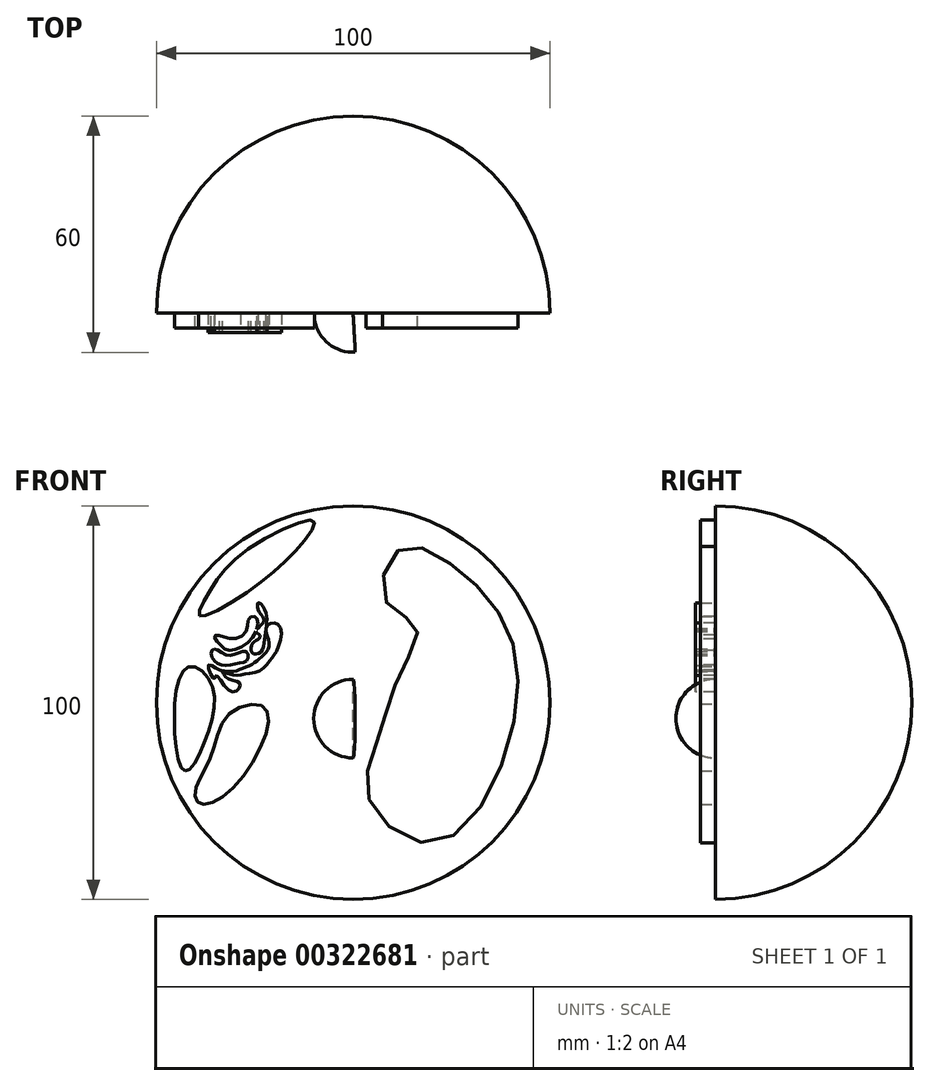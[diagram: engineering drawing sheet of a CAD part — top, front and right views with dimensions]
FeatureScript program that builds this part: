
annotation { "Feature Type Name" : "Feature", "Feature Type Description" : "" }
export const myFeature = defineFeature(function(context is Context, id is Id, definition is map)
    precondition{}
    {
        {
            var Q0;
            Q0=qCreatedBy(makeId("Front.planeOp"),FACE);
            var sketch = newSketch(context, id + "F0", { "sketchPlane" : qUnion([Q0])});
            skLineSegment(sketch, "E0", {"start": v(0, 0) * mm, "end": v(0, 100) * mm});
            skArc(sketch, "E1", {"start": v(0, 0) * mm, "mid": v(50, 50) * mm, "end": v(0, 100) * mm});
            skSolve(sketch);
        }
        {
            var Q0;
            Q0 = qSketchRegion(id + "F0", true);
            var Q1;
            Q1=makeQuery(id+"F0.imprint","IMPRINT",FACE,{"disambiguationData":[TD([[makeQuery(id+"F0.imprint","IMPRINT",EDGE,{"derivedFrom":sQuery(id+"F0.wireOp",EDGE,"E0")}),-1.0]])]});
            var Q2;
            Q2=sQuery(id+"F0.wireOp",EDGE,"E0");
            revolve(context, id + "F1", {"entities" : qUnion([Q0, Q1]), "axis" : qUnion([Q2]), "revolveType" : RevolveType.ONE_DIRECTION, "angle" : 180 * degree});
        }
        {
            var Q0;
            Q0=makeQuery(id+"F1.opRevolve","CAP_FACE",FACE,{"disambiguationData":[OSD([sQuery(id+"F0.wireOp",EDGE,"E0"),sQuery(id+"F0.wireOp",EDGE,"E1")])],"isStart":true});
            var sketch = newSketch(context, id + "F2", { "sketchPlane" : qUnion([Q0])});
            skLineSegment(sketch, "E2", {"start": v(0, 35.93) * mm, "end": v(0, 55.93) * mm});
            skArc(sketch, "E3", {"start": v(0, 55.93) * mm, "mid": v(-10, 45.93) * mm, "end": v(0, 35.93) * mm});
            skSolve(sketch);
        }
        {
            var Q0;
            Q0 = qSketchRegion(id + "F2", true);
            var Q1;
            Q1=sQuery(id+"F2.wireOp",EDGE,"E2");
            revolve(context, id + "F3", {"entities" : qUnion([Q0]), "axis" : qUnion([Q1]), "revolveType" : RevolveType.ONE_DIRECTION, "angle" : 93.1 * degree});
        }
        {
            var Q0;
            Q0=makeQuery(id+"F3.opRevolve","CAP_FACE",FACE,{"disambiguationData":[OSD([sQuery(id+"F2.wireOp",EDGE,"E2"),sQuery(id+"F2.wireOp",EDGE,"E3")])],"isStart":false});
            var sketch = newSketch(context, id + "F4", { "sketchPlane" : qUnion([Q0])});
            skLineSegment(sketch, "E4", {"start": v(0, 43.18) * mm, "end": v(0, 48.18) * mm});
            skArc(sketch, "E5", {"start": v(0, 48.18) * mm, "mid": v(-2.5, 45.68) * mm, "end": v(0, 43.18) * mm});
            skSolve(sketch);
        }
        {
            var Q0;
            Q0=sQuery(id+"F4.wireOp",EDGE,"E5");
            var Q1;
            Q1=sQuery(id+"F4.wireOp",EDGE,"E4");
            revolve(context, id + "F5", {"bodyType" : ToolBodyType.SURFACE, "surfaceEntities" : qUnion([Q0]), "axis" : qUnion([Q1]), "revolveType" : RevolveType.ONE_DIRECTION, "angle" : 86.48 * degree});
        }
        {
            var Q0;
            Q0=makeQuery(id+"F1.opRevolve","CAP_FACE",FACE,{"disambiguationData":[OSD([sQuery(id+"F0.wireOp",EDGE,"E0"),sQuery(id+"F0.wireOp",EDGE,"E1")])],"isStart":true});
            var sketch = newSketch(context, id + "F6", { "sketchPlane" : qUnion([Q0])});
            skLineSegment(sketch, "E6", {"start": v(-9.98, 15.87) * mm, "end": v(-9.98, 23.01) * mm});
            skArc(sketch, "E7", {"start": v(-9.98, 15.87) * mm, "mid": v(-6.4, 19.44) * mm, "end": v(-9.98, 23.01) * mm});
            skSolve(sketch);
        }
        {
            var Q0;
            Q0=sQuery(id+"F6.wireOp",EDGE,"E7");
            var Q1;
            Q1=sQuery(id+"F6.wireOp",EDGE,"E6");
            revolve(context, id + "F7", {"bodyType" : ToolBodyType.SURFACE, "surfaceEntities" : qUnion([Q0]), "axis" : qUnion([Q1]), "revolveType" : RevolveType.FULL});
        }
        {
            var Q0;
            Q0=makeQuery(id+"F1.opRevolve","CAP_FACE",FACE,{"disambiguationData":[OSD([sQuery(id+"F0.wireOp",EDGE,"E0"),sQuery(id+"F0.wireOp",EDGE,"E1")])],"isStart":true});
            var sketch = newSketch(context, id + "F8", { "sketchPlane" : qUnion([Q0])});
            skLineSegment(sketch, "E8", {"start": v(-1.05, 9.65) * mm, "end": v(-1.05, 18.62) * mm});
            skSolve(sketch);
        }
        {
            var Q0;
            Q0=makeQuery(id+"F8.imprint","IMPRINT",FACE,{"disambiguationData":[TD([[makeQuery(id+"F8.imprint","IMPRINT",EDGE,{"derivedFrom":makeQuery(id+"F1.opRevolve","CAP_EDGE",EDGE,{"disambiguationData":[OSD([sQuery(id+"F0.wireOp",EDGE,"E1")])],"isStart":true})}),-1.0]])]});
            var sketch = newSketch(context, id + "F9", { "sketchPlane" : qUnion([Q0])});
            skArc(sketch, "E9", {"start": v(-0.92, 9.35) * mm, "mid": v(3.57, 13.83) * mm, "end": v(-0.68, 18.54) * mm});
            skSolve(sketch);
        }
        {
            var Q0;
            Q0=sQuery(id+"F9.wireOp",EDGE,"E9");
            var Q1;
            Q1=sQuery(id+"F8.wireOp",EDGE,"E8");
            revolve(context, id + "F10", {"bodyType" : ToolBodyType.SURFACE, "surfaceEntities" : qUnion([Q0]), "axis" : qUnion([Q1]), "revolveType" : RevolveType.FULL});
        }
        {
            var Q0;
            Q0=makeQuery(id+"F1.opRevolve","CAP_FACE",FACE,{"disambiguationData":[OSD([sQuery(id+"F0.wireOp",EDGE,"E0"),sQuery(id+"F0.wireOp",EDGE,"E1")])],"isStart":true});
            var sketch = newSketch(context, id + "F11", { "sketchPlane" : qUnion([Q0])});
            skLineSegment(sketch, "E10", {"start": v(-5.22, 25.46) * mm, "end": v(-0.61, 21.85) * mm});
            skSolve(sketch);
        }
        {
            var Q0;
            Q0=makeQuery(id+"F11.imprint","IMPRINT",FACE,{"disambiguationData":[TD([[makeQuery(id+"F11.imprint","IMPRINT",EDGE,{"derivedFrom":makeQuery(id+"F1.opRevolve","CAP_EDGE",EDGE,{"disambiguationData":[OSD([sQuery(id+"F0.wireOp",EDGE,"E1")])],"isStart":true})}),-1.0]])]});
            var sketch = newSketch(context, id + "F12", { "sketchPlane" : qUnion([Q0])});
            skArc(sketch, "E11", {"start": v(-0.54, 22.14) * mm, "mid": v(-1.04, 25.86) * mm, "end": v(-4.8, 25.84) * mm});
            skSolve(sketch);
        }
        {
            var Q0;
            Q0=sQuery(id+"F12.wireOp",EDGE,"E11");
            var Q1;
            Q1=sQuery(id+"F11.wireOp",EDGE,"E10");
            revolve(context, id + "F13", {"bodyType" : ToolBodyType.SURFACE, "surfaceEntities" : qUnion([Q0]), "axis" : qUnion([Q1]), "revolveType" : RevolveType.FULL});
        }
        {
            var Q0;
            Q0=makeQuery(id+"F1.opRevolve","CAP_FACE",FACE,{"disambiguationData":[OSD([sQuery(id+"F0.wireOp",EDGE,"E0"),sQuery(id+"F0.wireOp",EDGE,"E1")])],"isStart":true});
            var sketch = newSketch(context, id + "F14", { "sketchPlane" : qUnion([Q0])});
            skLineSegment(sketch, "E12", {"start": v(-25.5, 15.6) * mm, "end": v(-20.36, 10.58) * mm});
            skSolve(sketch);
        }
        {
            var Q0;
            Q0=makeQuery(id+"F14.imprint","IMPRINT",FACE,{"disambiguationData":[TD([[makeQuery(id+"F14.imprint","IMPRINT",EDGE,{"derivedFrom":makeQuery(id+"F1.opRevolve","CAP_EDGE",EDGE,{"disambiguationData":[OSD([sQuery(id+"F0.wireOp",EDGE,"E1")])],"isStart":true})}),-1.0]])]});
            var sketch = newSketch(context, id + "F15", { "sketchPlane" : qUnion([Q0])});
            skArc(sketch, "E13", {"start": v(-20.16, 10.62) * mm, "mid": v(-20.3, 15.55) * mm, "end": v(-25.24, 15.58) * mm});
            skSolve(sketch);
        }
        {
            var Q0;
            Q0=sQuery(id+"F15.wireOp",EDGE,"E13");
            var Q1;
            Q1=sQuery(id+"F14.wireOp",EDGE,"E12");
            revolve(context, id + "F16", {"bodyType" : ToolBodyType.SURFACE, "surfaceEntities" : qUnion([Q0]), "axis" : qUnion([Q1]), "revolveType" : RevolveType.FULL});
        }
        {
            var Q0;
            Q0=makeQuery(id+"F1.opRevolve","CAP_FACE",FACE,{"disambiguationData":[OSD([sQuery(id+"F0.wireOp",EDGE,"E0"),sQuery(id+"F0.wireOp",EDGE,"E1")])],"isStart":true});
            var sketch = newSketch(context, id + "F17", { "sketchPlane" : qUnion([Q0])});
            skFitSpline(sketch, "E14", {"points": [v(3.98, 25.41) * mm, v(6.33, 40.73) * mm, v(11.83, 57.14) * mm, v(16.09, 69.44) * mm, v(8.24, 75.74) * mm, v(11.77, 88.87) * mm, v(25.32, 84.86) * mm, v(39.63, 67.79) * mm, v(39.35, 39.17) * mm, v(21.03, 14.43) * mm, v(3.98, 25.41) * mm]});
            skSolve(sketch);
        }
        {
            var Q0;
            Q0 = qSketchRegion(id + "F17", true);
            extrude(context, id + "F18", {"entities" : qUnion([Q0]), "depth" : 3.8 * mm});
        }
        {
            var Q0;
            Q0=makeQuery(id+"F1.opRevolve","CAP_FACE",FACE,{"disambiguationData":[OSD([sQuery(id+"F0.wireOp",EDGE,"E0"),sQuery(id+"F0.wireOp",EDGE,"E1")])],"isStart":true});
            var sketch = newSketch(context, id + "F19", { "sketchPlane" : qUnion([Q0])});
            skFitSpline(sketch, "E15", {"points": [v(-5.34, 33.82) * mm, v(-10.76, 39.31) * mm, v(-11.9, 50.03) * mm, v(-6.84, 56.99) * mm, v(-0.98, 58.02) * mm, v(-4.17, 59.69) * mm, v(-11.54, 54.89) * mm, v(-13.42, 44.76) * mm, v(-14.17, 47.53) * mm, v(-11.8, 56.36) * mm, v(-6.12, 61.62) * mm, v(-9.56, 60.77) * mm, v(-15.66, 50) * mm, v(-10.71, 37.15) * mm, v(-4, 29.35) * mm, v(-9.47, 31.84) * mm, v(-14.84, 39.25) * mm, v(-13.36, 32.71) * mm, v(-8.21, 28.94) * mm, v(-13.58, 29.53) * mm, v(-16.7, 36.95) * mm, v(-16.6, 45.1) * mm, v(-16.43, 53.1) * mm, v(-18, 50.07) * mm, v(-17.77, 35.45) * mm, v(-19.26, 40.83) * mm, v(-19.08, 48.83) * mm, v(-17.32, 56.78) * mm, v(-14.53, 58.9) * mm], "startDerivative": vector(-170.77, 125.27) * mm, "endDerivative": vector(126.65, 58.6) * mm});
            skSolve(sketch);
        }
        {
            var Q0;
            Q0=sQuery(id+"F19.wireOp",EDGE,"E15");
            extrude(context, id + "F20", {"bodyType" : ToolBodyType.SURFACE, "surfaceEntities" : qUnion([Q0]), "depth" : 3.8 * mm});
        }
        {
            var Q0;
            Q0=makeQuery(id+"F1.opRevolve","CAP_FACE",FACE,{"disambiguationData":[OSD([sQuery(id+"F0.wireOp",EDGE,"E0"),sQuery(id+"F0.wireOp",EDGE,"E1")])],"isStart":true});
            var sketch = newSketch(context, id + "F21", { "sketchPlane" : qUnion([Q0])});
            skFitSpline(sketch, "E16", {"points": [v(-42.72, 32.63) * mm, v(-45.42, 46.17) * mm, v(-41.85, 59.09) * mm, v(-35.9, 54.62) * mm, v(-37.85, 39.7) * mm, v(-42.72, 32.63) * mm]});
            skSolve(sketch);
        }
        {
            var Q0;
            Q0=makeQuery(id+"F21.imprint","IMPRINT",FACE,{"disambiguationData":[TD([[makeQuery(id+"F21.imprint","IMPRINT",EDGE,{"derivedFrom":sQuery(id+"F21.wireOp",EDGE,"E16")}),-1.0]])]});
            extrude(context, id + "F22", {"entities" : qUnion([Q0]), "operationType" : NewBodyOperationType.ADD, "depth" : 3.8 * mm});
        }
        {
            var Q0;
            Q0=makeQuery(id+"F22.opExtrude","CAP_FACE",FACE,{"disambiguationData":[OSD([sQuery(id+"F21.wireOp",EDGE,"E16")])],"isStart":false});
            var sketch = newSketch(context, id + "F23", { "sketchPlane" : qUnion([Q0])});
            skFitSpline(sketch, "E17", {"points": [v(-44.45, 35.83) * mm, v(-39.84, 35.45) * mm, v(-44.93, 38.4) * mm, v(-40.6, 40) * mm, v(-42.75, 43.08) * mm, v(-36.55, 43.22) * mm, v(-45.42, 46.7) * mm, v(-38.7, 47.88) * mm, v(-41.6, 51.98) * mm, v(-35.66, 53.96) * mm, v(-43.99, 56.6) * mm, v(-38.47, 58.07) * mm], "startDerivative": vector(97, -15.74) * mm, "endDerivative": vector(108.18, 13.67) * mm});
            skSolve(sketch);
        }
        {
            var Q0;
            Q0=sQuery(id+"F23.wireOp",EDGE,"E17");
            extrude(context, id + "F24", {"bodyType" : ToolBodyType.SURFACE, "surfaceEntities" : qUnion([Q0]), "depth" : 1.27 * mm});
        }
        {
            var Q0;
            Q0=makeQuery(id+"F1.opRevolve","CAP_FACE",FACE,{"disambiguationData":[OSD([sQuery(id+"F0.wireOp",EDGE,"E0"),sQuery(id+"F0.wireOp",EDGE,"E1")])],"isStart":true});
            var sketch = newSketch(context, id + "F25", { "sketchPlane" : qUnion([Q0])});
            skFitSpline(sketch, "E18", {"points": [v(-39.84, 28.43) * mm, v(-36, 36.67) * mm, v(-31.42, 47.17) * mm, v(-22.72, 48.95) * mm, v(-22.91, 39.98) * mm, v(-33.71, 25.64) * mm, v(-39.36, 24.6) * mm, v(-39.84, 28.43) * mm]});
            skSolve(sketch);
        }
        {
            var Q0;
            Q0=makeQuery(id+"F25.imprint","IMPRINT",FACE,{"disambiguationData":[TD([[makeQuery(id+"F25.imprint","IMPRINT",EDGE,{"derivedFrom":sQuery(id+"F25.wireOp",EDGE,"E18")}),-1.0]])]});
            extrude(context, id + "F26", {"entities" : qUnion([Q0]), "operationType" : NewBodyOperationType.ADD, "depth" : 3.8 * mm});
        }
        {
            var Q0;
            Q0=makeQuery(id+"F26.opExtrude","CAP_FACE",FACE,{"disambiguationData":[OSD([sQuery(id+"F25.wireOp",EDGE,"E18")])],"isStart":false});
            var sketch = newSketch(context, id + "F27", { "sketchPlane" : qUnion([Q0])});
            skFitSpline(sketch, "E19", {"points": [v(-37.4, 26.99) * mm, v(-32.87, 26.22) * mm, v(-36.33, 30.35) * mm, v(-37.45, 33.54) * mm, v(-34.01, 32.77) * mm, v(-29.44, 29.45) * mm, v(-29.9, 34.42) * mm, v(-36.04, 36.59) * mm, v(-35.2, 39.2) * mm, v(-25.56, 34.76) * mm, v(-28.54, 40.27) * mm, v(-33.94, 43.19) * mm, v(-29.7, 44.09) * mm, v(-23.11, 39.5) * mm, v(-26.04, 46.6) * mm, v(-28.19, 49.06) * mm], "startDerivative": vector(106.41, -30.59) * mm, "endDerivative": vector(-35.96, 28.76) * mm});
            skSolve(sketch);
        }
        {
            var Q0;
            Q0=sQuery(id+"F27.wireOp",EDGE,"E19");
            extrude(context, id + "F28", {"bodyType" : ToolBodyType.SURFACE, "surfaceEntities" : qUnion([Q0]), "depth" : 1.27 * mm});
        }
        {
            var Q0;
            Q0=makeQuery(id+"F1.opRevolve","CAP_FACE",FACE,{"disambiguationData":[OSD([sQuery(id+"F0.wireOp",EDGE,"E0"),sQuery(id+"F0.wireOp",EDGE,"E1")])],"isStart":true});
            var sketch = newSketch(context, id + "F29", { "sketchPlane" : qUnion([Q0])});
            skFitSpline(sketch, "E20", {"points": [v(-39.07, 72.03) * mm, v(-27.03, 78) * mm, v(-13.06, 90.32) * mm, v(-10.1, 96.19) * mm, v(-27.32, 88.55) * mm, v(-36.71, 77.84) * mm, v(-39.07, 72.03) * mm]});
            skSolve(sketch);
        }
        {
            var Q0;
            Q0=makeQuery(id+"F29.imprint","IMPRINT",FACE,{"disambiguationData":[TD([[makeQuery(id+"F29.imprint","IMPRINT",EDGE,{"derivedFrom":sQuery(id+"F29.wireOp",EDGE,"E20")}),1.0]])]});
            extrude(context, id + "F30", {"entities" : qUnion([Q0]), "operationType" : NewBodyOperationType.ADD, "depth" : 3.8 * mm});
        }
        {
            var Q0;
            Q0=makeQuery(id+"F30.opExtrude","CAP_FACE",FACE,{"disambiguationData":[OSD([sQuery(id+"F29.wireOp",EDGE,"E20")])],"isStart":false});
            var sketch = newSketch(context, id + "F31", { "sketchPlane" : qUnion([Q0])});
            skLineSegment(sketch, "E21", {"start": v(-34.1, 77.25) * mm, "end": v(-25.11, 81.46) * mm});
            skSolve(sketch);
        }
        {
            var Q0;
            Q0=sQuery(id+"F31.wireOp",EDGE,"E21");
            extrude(context, id + "F32", {"bodyType" : ToolBodyType.SURFACE, "surfaceEntities" : qUnion([Q0]), "depth" : 1.27 * mm});
        }
        {
            var Q0;
            Q0=makeQuery(id+"F30.opExtrude","CAP_FACE",FACE,{"disambiguationData":[OSD([sQuery(id+"F29.wireOp",EDGE,"E20")])],"isStart":false});
            var sketch = newSketch(context, id + "F33", { "sketchPlane" : qUnion([Q0])});
            skLineSegment(sketch, "E22", {"start": v(-29.6, 81.59) * mm, "end": v(-21.71, 89.22) * mm});
            skSolve(sketch);
        }
        {
            var Q0;
            Q0=sQuery(id+"F33.wireOp",EDGE,"E22");
            extrude(context, id + "F34", {"bodyType" : ToolBodyType.SURFACE, "surfaceEntities" : qUnion([Q0]), "depth" : 1.27 * mm});
        }
        {
            var Q0;
            Q0=makeQuery(id+"F30.opExtrude","CAP_FACE",FACE,{"disambiguationData":[OSD([sQuery(id+"F29.wireOp",EDGE,"E20")])],"isStart":false});
            var sketch = newSketch(context, id + "F35", { "sketchPlane" : qUnion([Q0])});
            skLineSegment(sketch, "E23", {"start": v(-22.2, 84.96) * mm, "end": v(-15.3, 92.43) * mm});
            skSolve(sketch);
        }
        {
            var Q0;
            Q0=sQuery(id+"F35.wireOp",EDGE,"E23");
            extrude(context, id + "F36", {"bodyType" : ToolBodyType.SURFACE, "surfaceEntities" : qUnion([Q0]), "depth" : 1.27 * mm});
        }
        {
            var Q0;
            Q0=makeQuery(id+"F1.opRevolve","CAP_FACE",FACE,{"disambiguationData":[OSD([sQuery(id+"F0.wireOp",EDGE,"E0"),sQuery(id+"F0.wireOp",EDGE,"E1")])],"isStart":true});
            var sketch = newSketch(context, id + "F37", { "sketchPlane" : qUnion([Q0])});
            skFitSpline(sketch, "E24", {"points": [v(-12.18, 76.99) * mm, v(-7.75, 76.03) * mm, v(-2.11, 75.45) * mm, v(4.17, 77.2) * mm, v(-0.14, 77.83) * mm, v(-4.6, 77.14) * mm, v(-10.38, 78.87) * mm, v(-7.1, 79.1) * mm, v(-2.17, 78.62) * mm, v(-5.6, 80.36) * mm, v(-13.67, 81.19) * mm, v(-12.37, 82.31) * mm, v(-8.1, 82.05) * mm, v(-0.52, 80.2) * mm, v(4.46, 80.1) * mm, v(-2.55, 82.27) * mm, v(-9.33, 83.49) * mm, v(-14.98, 83.6) * mm, v(-11.06, 85.17) * mm, v(-1.82, 83.08) * mm, v(4.81, 81.55) * mm], "startDerivative": vector(97.6, -20.31) * mm, "endDerivative": vector(112.55, -20.12) * mm});
            skSolve(sketch);
        }
        {
            var Q0;
            Q0=sQuery(id+"F37.wireOp",EDGE,"E24");
            extrude(context, id + "F38", {"bodyType" : ToolBodyType.SURFACE, "surfaceEntities" : qUnion([Q0]), "depth" : 3.8 * mm});
        }
        {
            var Q0;
            Q0=makeQuery(id+"F1.opRevolve","CAP_FACE",FACE,{"disambiguationData":[OSD([sQuery(id+"F0.wireOp",EDGE,"E0"),sQuery(id+"F0.wireOp",EDGE,"E1")])],"isStart":true});
            var sketch = newSketch(context, id + "F39", { "sketchPlane" : qUnion([Q0])});
            skPoint(sketch, "E25", {"position": v(-15.56, 42.29) * mm});
            skPoint(sketch, "E26", {"position": v(-13.43, 38.95) * mm});
            skPoint(sketch, "E27", {"position": v(-16.7, 46.14) * mm});
            skPoint(sketch, "E28", {"position": v(-16.8, 48.5) * mm});
            skPoint(sketch, "E29", {"position": v(-16.5, 51) * mm});
            skPoint(sketch, "E30", {"position": v(-15.7, 53.42) * mm});
            skPoint(sketch, "E31", {"position": v(-15, 50.44) * mm});
            skPoint(sketch, "E32", {"position": v(-19.22, 43.78) * mm});
            skPoint(sketch, "E33", {"position": v(-19.3, 46.37) * mm});
            skPoint(sketch, "E34", {"position": v(-18.86, 49.48) * mm});
            skPoint(sketch, "E35", {"position": v(-19.3, 40.7) * mm});
            skPoint(sketch, "E36", {"position": v(-20.4, 39.28) * mm});
            skPoint(sketch, "E37", {"position": v(-20.64, 42.15) * mm});
            skPoint(sketch, "E38", {"position": v(-20.66, 45.06) * mm});
            skPoint(sketch, "E39", {"position": v(-20.12, 50.34) * mm});
            skPoint(sketch, "E40", {"position": v(-19.32, 53.73) * mm});
            skPoint(sketch, "E41", {"position": v(-17.82, 39.02) * mm});
            skPoint(sketch, "E42", {"position": v(-17.9, 42.54) * mm});
            skPoint(sketch, "E43", {"position": v(-18.05, 36.78) * mm});
            skPoint(sketch, "E44", {"position": v(-17.52, 33.7) * mm});
            skPoint(sketch, "E45", {"position": v(-15.8, 34.68) * mm});
            skPoint(sketch, "E46", {"position": v(-16.37, 36.65) * mm});
            skPoint(sketch, "E47", {"position": v(-14.86, 37.8) * mm});
            skPoint(sketch, "E48", {"position": v(-13.77, 35.87) * mm});
            skPoint(sketch, "E49", {"position": v(-12.6, 33.68) * mm});
            skPoint(sketch, "E50", {"position": v(-8.21, 35.05) * mm});
            skPoint(sketch, "E51", {"position": v(-10.77, 37.37) * mm});
            skPoint(sketch, "E52", {"position": v(-12.36, 40.37) * mm});
            skPoint(sketch, "E53", {"position": v(-13.11, 43.04) * mm});
            skPoint(sketch, "E54", {"position": v(-13.39, 46.03) * mm});
            skPoint(sketch, "E55", {"position": v(-13.2, 48.62) * mm});
            skPoint(sketch, "E56", {"position": v(-15.11, 48.07) * mm});
            skPoint(sketch, "E57", {"position": v(-12.26, 51.64) * mm});
            skPoint(sketch, "E58", {"position": v(-11.14, 53.81) * mm});
            skPoint(sketch, "E59", {"position": v(-14.57, 52.76) * mm});
            skPoint(sketch, "E60", {"position": v(-15.12, 55.14) * mm});
            skPoint(sketch, "E61", {"position": v(-12.19, 36.62) * mm});
            skPoint(sketch, "E62", {"position": v(-10.46, 34.6) * mm});
            skPoint(sketch, "E63", {"position": v(-17.15, 32.12) * mm});
            skPoint(sketch, "E64", {"position": v(-16.16, 30.49) * mm});
            skPoint(sketch, "E65", {"position": v(-14.55, 29.13) * mm});
            skPoint(sketch, "E66", {"position": v(-12.66, 28.54) * mm});
            skPoint(sketch, "E67", {"position": v(-12.01, 30.37) * mm});
            skPoint(sketch, "E68", {"position": v(-14.54, 32.42) * mm});
            skPoint(sketch, "E69", {"position": v(-10.74, 29.4) * mm});
            skPoint(sketch, "E70", {"position": v(-8.41, 29.85) * mm});
            skPoint(sketch, "E71", {"position": v(-10.93, 31.67) * mm});
            skPoint(sketch, "E72", {"position": v(-5.95, 30.37) * mm});
            skPoint(sketch, "E73", {"position": v(-8.04, 32.66) * mm});
            skPoint(sketch, "E74", {"position": v(-12.53, 54.62) * mm});
            skPoint(sketch, "E75", {"position": v(-10.27, 55.05) * mm});
            skPoint(sketch, "E76", {"position": v(-11.52, 56.48) * mm});
            skPoint(sketch, "E77", {"position": v(-13.85, 56.92) * mm});
            skPoint(sketch, "E78", {"position": v(-12.93, 58.2) * mm});
            skPoint(sketch, "E79", {"position": v(-5.63, 59.2) * mm});
            skPoint(sketch, "E80", {"position": v(-3.77, 59.2) * mm});
            skPoint(sketch, "E81", {"position": v(-2.69, 58.13) * mm});
            skPoint(sketch, "E82", {"position": v(-7.66, 61.14) * mm});
            skSolve(sketch);
        }
        {
            var Q0;
            Q0=makeQuery(id+"F39.imprint","IMPRINT",FACE,{"disambiguationData":[TD([[makeQuery(id+"F39.imprint","IMPRINT",EDGE,{"derivedFrom":makeQuery(id+"F1.opRevolve","CAP_EDGE",EDGE,{"disambiguationData":[OSD([sQuery(id+"F0.wireOp",EDGE,"E1")])],"isStart":true})}),-1.0]])]});
            var sketch = newSketch(context, id + "F40", { "sketchPlane" : qUnion([Q0])});
            skFitSpline(sketch, "E83", {"points": [v(-34.32, 67.15) * mm, v(-30.95, 66.22) * mm, v(-27.27, 67.99) * mm, v(-26.42, 71.4) * mm, v(-24.82, 71.8) * mm, v(-24.24, 69.59) * mm, v(-26.67, 65.28) * mm, v(-31.5, 63.27) * mm, v(-33.86, 64.83) * mm, v(-35.22, 66.77) * mm, v(-34.32, 67.15) * mm]});
            skFitSpline(sketch, "E84", {"points": [v(-35.29, 63.62) * mm, v(-32.46, 62.21) * mm, v(-29.54, 62.41) * mm, v(-27, 62.84) * mm, v(-26.82, 60.86) * mm, v(-28.67, 60.1) * mm, v(-32.13, 59.4) * mm, v(-34.96, 60.3) * mm, v(-36.05, 62.68) * mm, v(-35.29, 63.62) * mm]});
            skFitSpline(sketch, "E85", {"points": [v(-25.32, 65.3) * mm, v(-25.94, 63.86) * mm, v(-25.53, 62.54) * mm, v(-23.7, 62.63) * mm, v(-22.61, 65.15) * mm, v(-22.17, 68.85) * mm, v(-22.2, 72.95) * mm, v(-24.07, 75.36) * mm, v(-24.2, 73.77) * mm, v(-22.75, 71.38) * mm, v(-23.08, 69.98) * mm, v(-24.68, 68.03) * mm, v(-23.7, 67.2) * mm, v(-24, 66.16) * mm, v(-25.32, 65.3) * mm]});
            skFitSpline(sketch, "E86", {"points": [v(-30.64, 57) * mm, v(-33.92, 58.25) * mm, v(-31.21, 57.86) * mm, v(-28.24, 58.61) * mm, v(-25.6, 59.75) * mm, v(-23.82, 61.14) * mm, v(-21.93, 62.98) * mm, v(-21.4, 65.65) * mm, v(-22.17, 68.85) * mm, v(-20.56, 70.25) * mm, v(-18.37, 68.85) * mm, v(-19.57, 62.88) * mm, v(-21.01, 60.8) * mm, v(-23.63, 58.1) * mm, v(-27.85, 57.16) * mm, v(-30.64, 57) * mm]});
            skFitSpline(sketch, "E87", {"points": [v(-32, 56.17) * mm, v(-28.94, 55.09) * mm, v(-28.93, 53.63) * mm, v(-31.3, 52.95) * mm, v(-34.86, 56.88) * mm, v(-35.3, 56.05) * mm, v(-36.78, 59.47) * mm, v(-33.92, 58.25) * mm, v(-33.22, 57.87) * mm, v(-32, 56.17) * mm]});
            skFitSpline(sketch, "E88", {"points": [v(-21.47, 75.89) * mm, v(-20.74, 73.63) * mm, v(-19.36, 72.12) * mm, v(-17.58, 72.7) * mm, v(-17.39, 75.02) * mm, v(-18.7, 76.85) * mm], "startDerivative": vector(2.84, -10.94) * mm, "endDerivative": vector(-7.78, 7.97) * mm});
            skFitSpline(sketch, "E89", {"points": [v(-21.41, 75.16) * mm, v(-22.1, 77.33) * mm, v(-18.7, 76.85) * mm], "startDerivative": vector(-3.25, 6.13) * mm, "endDerivative": vector(8.27, -2.45) * mm});
            skSolve(sketch);
        }
        {
            var Q0;
            Q0 = qSketchRegion(id + "F40", true);
            extrude(context, id + "F41", {"entities" : qUnion([Q0]), "depth" : 5 * mm});
        }
    });
